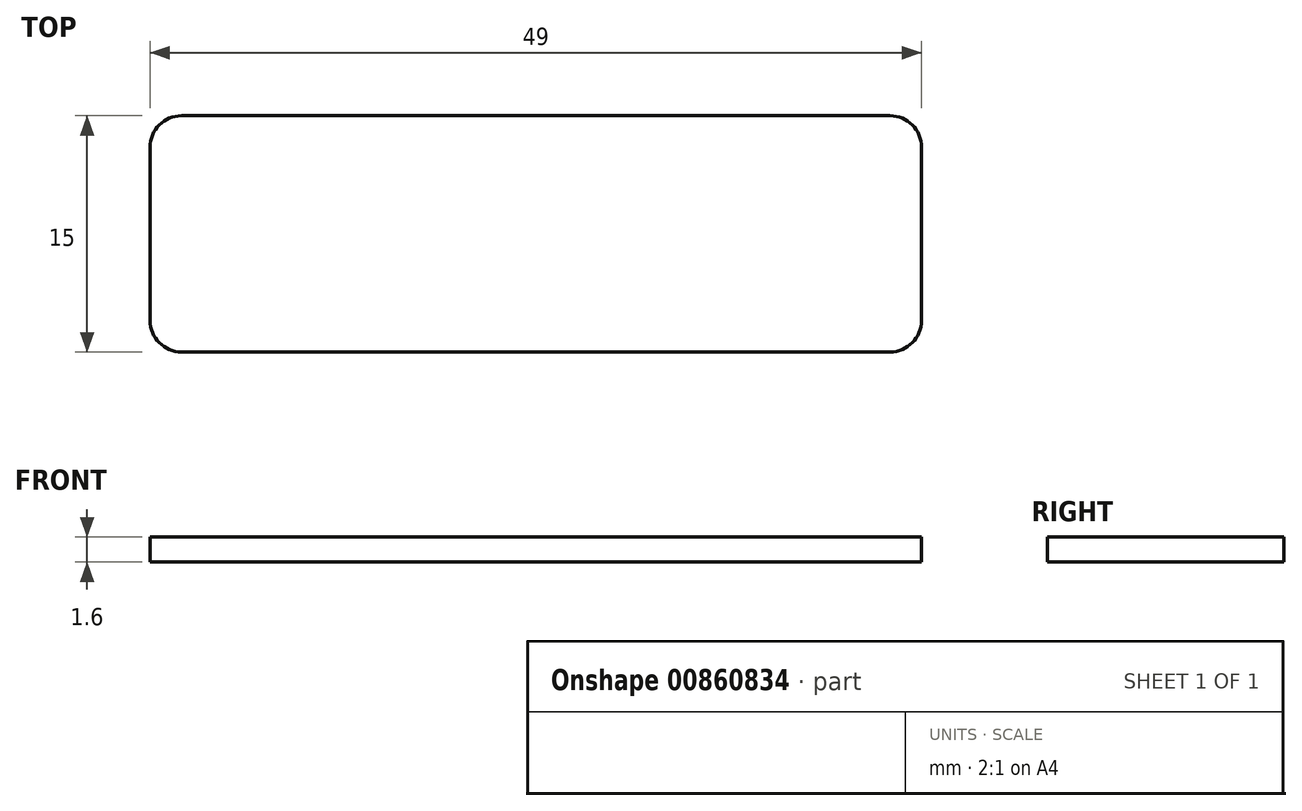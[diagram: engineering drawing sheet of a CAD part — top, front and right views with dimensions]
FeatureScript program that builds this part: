
annotation { "Feature Type Name" : "Feature", "Feature Type Description" : "" }
export const myFeature = defineFeature(function(context is Context, id is Id, definition is map)
    precondition{}
    {
        {
            var Q0;
            Q0=qCreatedBy(makeId("Top.planeOp"),FACE);
            var sketch = newSketch(context, id + "F0", { "sketchPlane" : qUnion([Q0])});
            skLineSegment(sketch, "E0.bottom", {"start": v(24.5, -7.5) * mm, "end": v(-24.5, -7.5) * mm});
            skLineSegment(sketch, "E0.top", {"start": v(24.5, 7.5) * mm, "end": v(-24.5, 7.5) * mm});
            skLineSegment(sketch, "E0.left", {"start": v(24.5, -7.5) * mm, "end": v(24.5, 7.5) * mm});
            skLineSegment(sketch, "E0.right", {"start": v(-24.5, -7.5) * mm, "end": v(-24.5, 7.5) * mm});
            skPoint(sketch, "E0.middle", {"position": v(0, 0) * mm});
            skSolve(sketch);
        }
        {
            var Q0;
            Q0 = qSketchRegion(id + "F0", true);
            extrude(context, id + "F1", {"entities" : qUnion([Q0]), "depth" : 1.6 * mm, "offsetDistance" : 25 * mm});
        }
        {
            var Q0;
            Q0=makeQuery(id+"F1.opExtrude","SWEPT_EDGE",EDGE,{"disambiguationData":[OSD([sQuery(id+"F0.wireOp",EDGE,"E0.bottom"),sQuery(id+"F0.wireOp",EDGE,"E0.left")])]});
            var Q1;
            Q1=makeQuery(id+"F1.opExtrude","SWEPT_EDGE",EDGE,{"disambiguationData":[OSD([sQuery(id+"F0.wireOp",EDGE,"E0.bottom"),sQuery(id+"F0.wireOp",EDGE,"E0.right")])]});
            var Q2;
            Q2=makeQuery(id+"F1.opExtrude","SWEPT_EDGE",EDGE,{"disambiguationData":[OSD([sQuery(id+"F0.wireOp",EDGE,"E0.top"),sQuery(id+"F0.wireOp",EDGE,"E0.right")])]});
            var Q3;
            Q3=makeQuery(id+"F1.opExtrude","SWEPT_EDGE",EDGE,{"disambiguationData":[OSD([sQuery(id+"F0.wireOp",EDGE,"E0.top"),sQuery(id+"F0.wireOp",EDGE,"E0.left")])]});
            fillet(context, id + "F2", {"entities" : qUnion([Q0, Q1, Q2, Q3]), "radius" : 2 * mm, "tangentPropagation" : true, "allowEdgeOverflow" : false});
        }
    });
